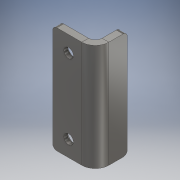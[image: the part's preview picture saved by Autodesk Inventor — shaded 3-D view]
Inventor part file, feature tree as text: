
AUTODESK INVENTOR PART (.ipt)
format: ipt  version: 2017 (Build 210142000, 142)  size: 178,176 bytes
history: native  units: mm
features: sheet_metal_op x3, sketch x2, other x2, fillet x1, extrude x1, chamfer x1
ambient origin geometry x8: Origin, YZ Plane, XZ Plane, XY Plane, X Axis, Y Axis, Z Axis, Center Point
bodies: Solid1 (feature_tree)
feature tree (10):
  sheet_metal_op  "Contour Flange1"
  fillet  "Fillet1"  Radius=15.0mm
  extrude  "Extrusion1"  Depth=3.175mm
  chamfer  "Chamfer1"  Distance=6.35mm
  sketch  "Sketch1"  dims[d1=20.0mm d2=3.175mm]
  other  "Plate1"
  sheet_metal_op  "Bend1"
  sheet_metal_op  "Corner1"
  sketch  "Sketch2"  dims[d3=1.5875mm d4=6.35mm d5=3.175mm d6=50.0mm d7=3.175mm d8=0.5mm d9=12.7mm d10=3.175mm d11=3.175mm d12=2.0mm d13=4.5mm d14=4.5mm d15=7.5mm d16=7.5mm d17=7.5mm d18=10.0mm d19=0.0mm d20=1.5mm d21=2.0mm d22=45.0deg]
  other  "Definition1"
